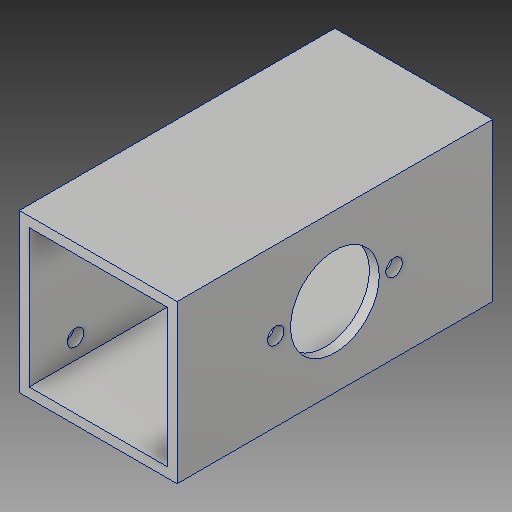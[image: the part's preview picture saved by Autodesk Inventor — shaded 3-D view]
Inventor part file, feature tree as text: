
AUTODESK INVENTOR PART (.ipt)
format: ipt  version: 2019 (Build 230136000, 136)  size: 148,480 bytes
history: native  units: in
note: dims shown in document units (in); Inventor stores cm internally (conversion verified against a paired STEP export)
features: reference x5, extrude x4, sketch x4, other x4
ambient origin geometry x8: Origin, YZ Plane, XZ Plane, XY Plane, X Axis, Y Axis, Z Axis, Center Point
bodies: Solid1 (feature_tree)
feature tree (17):
  extrude  "Extrusion1"  Depth=0.125in
  extrude  "Extrusion7"  Depth=2.0in
  extrude  "Extrusion8"  Depth=0.125in
  extrude  "Extrusion9"  Depth=1.0in TaperAngle=0.0deg
  sketch  "Sketch1"  dims[d0=2.0in d1=0.125in]
  sketch  "Sketch6"  dims[d2=4.0in d3=0.0in d11=2.0in]
  sketch  "Sketch7"  dims[d12=0.125in d23=1.125in]
  reference  "Reference2"
  reference  "Reference3"
  reference  "Reference4"
  reference  "Reference5"
  sketch  "Sketch8"  dims[d24=1.0in d25=0.0in d26=1.0in d27=0.0in d28=0.25in d29=0.437in d30=0.21in d31=1.0in d32=0.0in]
  reference  "Reference6"
  parser-record x1  (decoder bookkeeping rows leaked as tree rows — omitted from the tree; the rows remain in map.json)
  other  "Drive Arm.iam"
  other  "Arm 2 inch B:1"
  other  "Arm Bearing:1"
note: 1 file-system path scrubbed to <path> (originals preserved in map.json)
